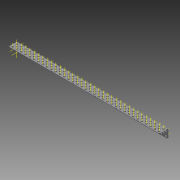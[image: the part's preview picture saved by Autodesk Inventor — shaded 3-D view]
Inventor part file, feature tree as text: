
AUTODESK INVENTOR PART (.ipt)
format: ipt  version: 2015 (Build 190159000, 159)  size: 2,328,064 bytes
history: native  units: in
note: dims shown in document units (in); Inventor stores cm internally (conversion verified against a paired STEP export)
features: other x215, pattern_linear x4, sheet_metal_op x1, extrude x1, imported_body x1, sketch x1
ambient origin geometry x8: Origin, YZ Plane, XZ Plane, XY Plane, X Axis, Y Axis, Z Axis, Center Point
bodies: Body1 (feature_tree)
feature tree (223):
  sheet_metal_op  "Fold1"
  other  "L-Channel"
  extrude  "length cut"  Depth=0.5in
  other  "top out axis"
  other  "top inner axis"
  other  "back out axis"
  other  "back inner axis"
  pattern_linear  "top outer axes"  Count1=2 Spacing1=0.5in
  pattern_linear  "top inner axes"  Spacing1=0.5in  [1 undecoded]
  pattern_linear  "back outer axes"  Count1=2 Spacing1=0.5in
  pattern_linear  "back inner axes"  Spacing1=0.5in  [1 undecoded]
  other  "right plane"
  imported_body  "Base1"
  sketch  "Sketch1"  dims[d1=0.0in d4=0.5in d5=0.7874in d7=0.5in d10=0.5in d13=0.5in d14=0.7874in d16=0.5in d19=0.5in d20=-17.5in d21=0.0in d22=0.0in d23=0.0in d24=0.0in d25=0.0in d26=0.0in]
  other  "Work Point1"
  other  "Work Point2"
  other  "Work Point3"
  other  "Work Point4"
  other  "Work Axis5"
  other  "Work Axis6"
  other  "Work Axis7"
  other  "Work Axis8"
  other  "Work Axis11"
  other  "Work Axis12"
  other  "Work Axis13"
  other  "Work Axis14"
  other  "Work Axis15"
  other  "Work Axis18"
  other  "Work Axis19"
  other  "Work Axis20"
  other  "Work Axis23"
  other  "Work Axis24"
  other  "Work Axis25"
  other  "Work Axis26"
  other  "Work Axis29"
  other  "Work Axis30"
  other  "Work Axis31"
  other  "Work Axis32"
  other  "Work Axis33"
  other  "Work Axis36"
  other  "Work Axis37"
  other  "Work Axis38"
  other  "Work Axis41"
  other  "Work Axis42"
  other  "Work Axis43"
  other  "Work Axis44"
  other  "Work Axis45"
  other  "Work Axis46"
  other  "Work Axis47"
  other  "Work Axis48"
  other  "Work Axis49"
  other  "Work Axis50"
  other  "Work Axis51"
  other  "Work Axis52"
  other  "Work Axis53"
  other  "Work Axis54"
  other  "Work Axis55"
  other  "Work Axis56"
  other  "Work Axis57"
  other  "Work Axis58"
  other  "Work Axis59"
  other  "Work Axis60"
  other  "Work Axis61"
  other  "Work Axis62"
  other  "Work Axis63"
  other  "Work Axis64"
  other  "Work Axis65"
  other  "Work Axis66"
  other  "Work Axis67"
  other  "Work Axis68"
  other  "Work Axis69"
  other  "Work Axis70"
  other  "Work Axis71"
  other  "Work Axis72"
  other  "Work Axis73"
  other  "Work Axis74"
  other  "Work Axis75"
  other  "Work Axis76"
  other  "Work Axis77"
  other  "Work Axis78"
  other  "Work Axis79"
  other  "Work Axis80"
  other  "Work Axis81"
  other  "Work Axis82"
  other  "Work Axis83"
  other  "Work Axis84"
  other  "Work Axis85"
  other  "Work Axis86"
  other  "Work Axis87"
  other  "Work Axis88"
  other  "Work Axis89"
  other  "Work Axis90"
  other  "Work Axis91"
  other  "Work Axis92"
  other  "Work Axis93"
  other  "Work Axis94"
  other  "Work Axis95"
  other  "Work Axis96"
  other  "Work Axis97"
  other  "Work Axis98"
  other  "Work Axis99"
  other  "Work Axis100"
  other  "Work Axis101"
  other  "Work Axis102"
  other  "Work Axis103"
  other  "Work Axis104"
  other  "Work Axis105"
  other  "Work Axis106"
  other  "Work Axis107"
  other  "Work Axis108"
  other  "Work Axis109"
  other  "Work Axis110"
  other  "Work Axis111"
  other  "Work Axis112"
  other  "Work Axis113"
  other  "Work Axis114"
  other  "Work Axis115"
  other  "Work Axis116"
  other  "Work Axis117"
  other  "Work Axis118"
  other  "Work Axis119"
  other  "Work Axis120"
  other  "Work Axis121"
  other  "Work Axis122"
  other  "Work Axis123"
  other  "Work Axis124"
  other  "Work Axis125"
  other  "Work Axis126"
  other  "Work Axis127"
  other  "Work Axis128"
  other  "Work Axis129"
  other  "Work Axis130"
  other  "Work Axis131"
  other  "Work Axis132"
  other  "Work Axis133"
  other  "Work Axis134"
  other  "Work Axis135"
  other  "Work Axis136"
  other  "Work Axis137"
  other  "Work Axis138"
  other  "Work Axis139"
  other  "Work Axis140"
  other  "Work Axis141"
  other  "Work Axis142"
  other  "Work Axis143"
  other  "Work Axis144"
  other  "Work Axis145"
  other  "Work Axis146"
  other  "Work Axis147"
  other  "Work Axis148"
  other  "Work Axis149"
  other  "Work Axis150"
  other  "Work Axis151"
  other  "Work Axis152"
  other  "Work Axis153"
  other  "Work Axis154"
  other  "Work Axis155"
  other  "Work Axis156"
  other  "Work Axis157"
  other  "Work Axis158"
  other  "Work Axis159"
  other  "Work Axis160"
  other  "left plane"
  other  "Work Axis161"
  other  "Work Axis162"
  other  "Work Axis163"
  other  "Work Axis164"
  other  "Work Axis165"
  other  "Work Axis166"
  other  "Work Axis167"
  other  "Work Axis168"
  other  "Work Axis169"
  other  "Work Axis170"
  other  "Work Axis171"
  other  "Work Axis172"
  other  "Work Axis173"
  other  "Work Axis174"
  other  "Work Axis175"
  other  "Work Axis176"
  other  "Work Axis177"
  other  "Work Axis178"
  other  "Work Axis179"
  other  "Work Axis180"
  other  "Work Axis181"
  other  "Work Axis182"
  other  "Work Axis183"
  other  "Work Axis184"
  other  "Work Axis185"
  other  "Work Axis186"
  other  "Work Axis187"
  other  "Work Axis188"
  other  "Work Axis189"
  other  "Work Axis190"
  other  "Work Axis191"
  other  "Work Axis192"
  other  "Work Axis193"
  other  "Work Axis194"
  other  "Work Axis195"
  other  "Work Axis196"
  other  "Work Axis197"
  other  "Work Axis198"
  other  "Work Axis199"
  other  "Work Axis200"
  other  "Work Axis201"
  other  "Work Axis202"
  other  "Work Axis203"
  other  "Work Axis204"
  other  "Work Axis205"
  other  "Work Axis206"
  other  "Work Axis207"
  other  "Work Axis208"
  other  "Work Axis209"
  other  "Work Axis210"
  other  "Work Axis211"
  other  "Work Axis212"
  other  "Work Axis213"
  other  "Work Axis214"
  other  "Work Axis215"
  other  "Work Axis216"
  other  "Work Axis217"
  other  "Work Axis218"
  other  "Work Axis219"
  other  "Work Axis220"
note: 2 required parameter values undecoded (feature->parameter linkage not recoverable at this tier; creation-order binding heuristic only, values carry confidence <= 0.55)
